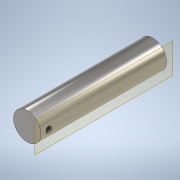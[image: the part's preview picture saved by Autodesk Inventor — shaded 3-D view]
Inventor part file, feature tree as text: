
AUTODESK INVENTOR PART (.ipt)
format: ipt  version: 2020 (Build 240168000, 168)  size: 109,568 bytes
history: native  units: mm
features: sketch x2, extrude x1, plane x1, hole x1
ambient origin geometry x8: Origin, YZ Plane, XZ Plane, XY Plane, X Axis, Y Axis, Z Axis, Center Point
bodies: Solid1 (feature_tree)
feature tree (5):
  extrude  "Extrusion1"  Depth=32.0mm TaperAngle=0.0deg
  plane  "Work Plane1"
  hole  "Hole1"  [1 undecoded]
  sketch  "Sketch1"  dims[d0=7.0mm d1=32.0mm d2=0.0mm]
  sketch  "Sketch2"  dims[d3=2.0mm d4=1.5mm d5=6.0mm d6=3.0mm d7=2.0mm d8=90.0deg d9=3.5mm d10=20.594885mm]
note: 1 required parameter value undecoded (feature->parameter linkage not recoverable at this tier; creation-order binding heuristic only, values carry confidence <= 0.55)
